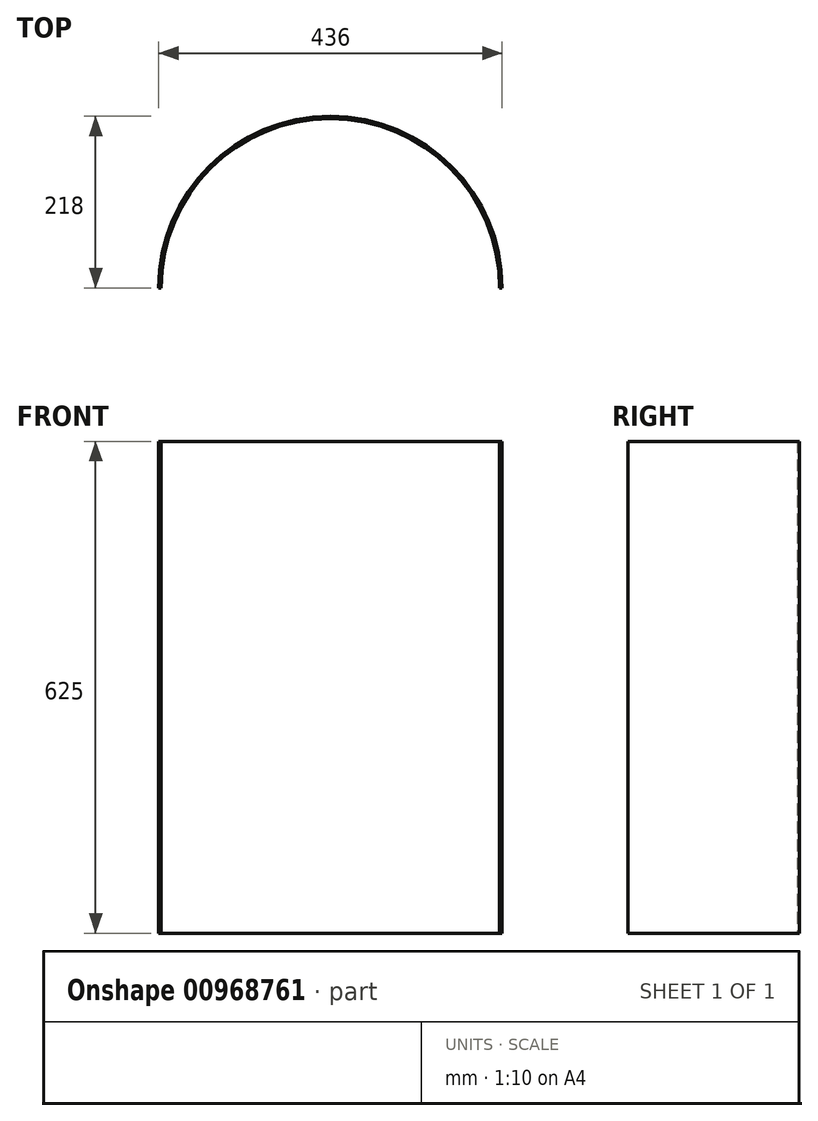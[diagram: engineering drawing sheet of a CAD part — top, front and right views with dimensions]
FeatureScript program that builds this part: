
annotation { "Feature Type Name" : "Feature", "Feature Type Description" : "" }
export const myFeature = defineFeature(function(context is Context, id is Id, definition is map)
    precondition{}
    {
        {
            var Q0;
            Q0=qCreatedBy(makeId("Top.planeOp"),FACE);
            var sketch = newSketch(context, id + "F0", { "sketchPlane" : qUnion([Q0])});
            skArc(sketch, "E0", {"start": v(215, 0) * mm, "mid": v(0, 215) * mm, "end": v(-215, 0) * mm});
            skArc(sketch, "E1", {"start": v(218, 0) * mm, "mid": v(0, 218) * mm, "end": v(-218, 0) * mm});
            skLineSegment(sketch, "E2", {"start": v(215, 0) * mm, "end": v(218, 0) * mm});
            skLineSegment(sketch, "E3", {"start": v(-215, 0) * mm, "end": v(-218, 0) * mm});
            skSolve(sketch);
        }
        {
            var Q0;
            Q0 = qSketchRegion(id + "F0", true);
            extrude(context, id + "F1", {"entities" : qUnion([Q0]), "depth" : 625 * mm, "offsetDistance" : 25 * mm});
        }
    });
